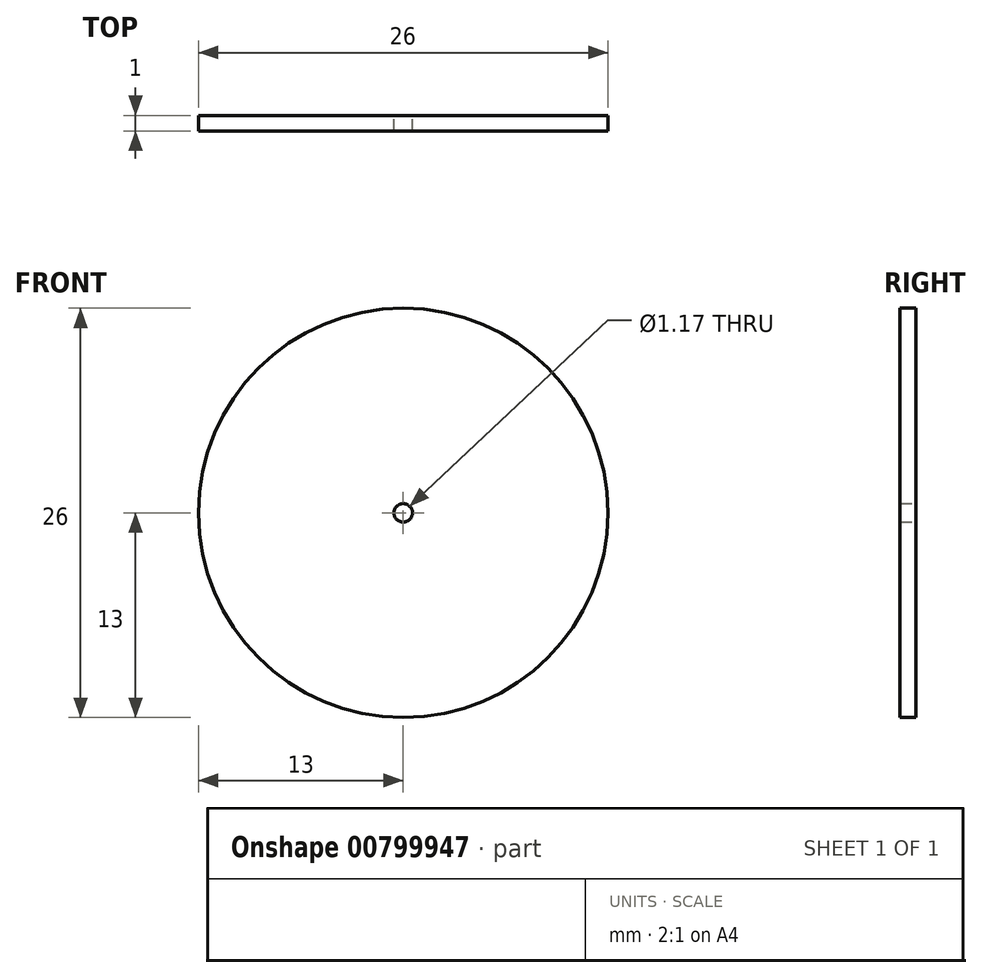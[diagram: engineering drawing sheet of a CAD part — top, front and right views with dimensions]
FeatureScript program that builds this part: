
annotation { "Feature Type Name" : "Feature", "Feature Type Description" : "" }
export const myFeature = defineFeature(function(context is Context, id is Id, definition is map)
    precondition{}
    {
        {
            var Q0;
            Q0=qCreatedBy(makeId("Front.planeOp"),FACE);
            var sketch = newSketch(context, id + "F0", { "sketchPlane" : qUnion([Q0])});
            skCircle(sketch, "E0", {"center": v(0, 0) * mm, "radius": 13 * mm});
            skCircle(sketch, "E1", {"center": v(0, 0) * mm, "radius": 0.59 * mm});
            skSolve(sketch);
        }
        {
            var Q0;
            Q0 = qSketchRegion(id + "F0", true);
            extrude(context, id + "F1", {"entities" : qUnion([Q0]), "depth" : 1 * mm, "offsetDistance" : 25 * mm});
        }
    });
